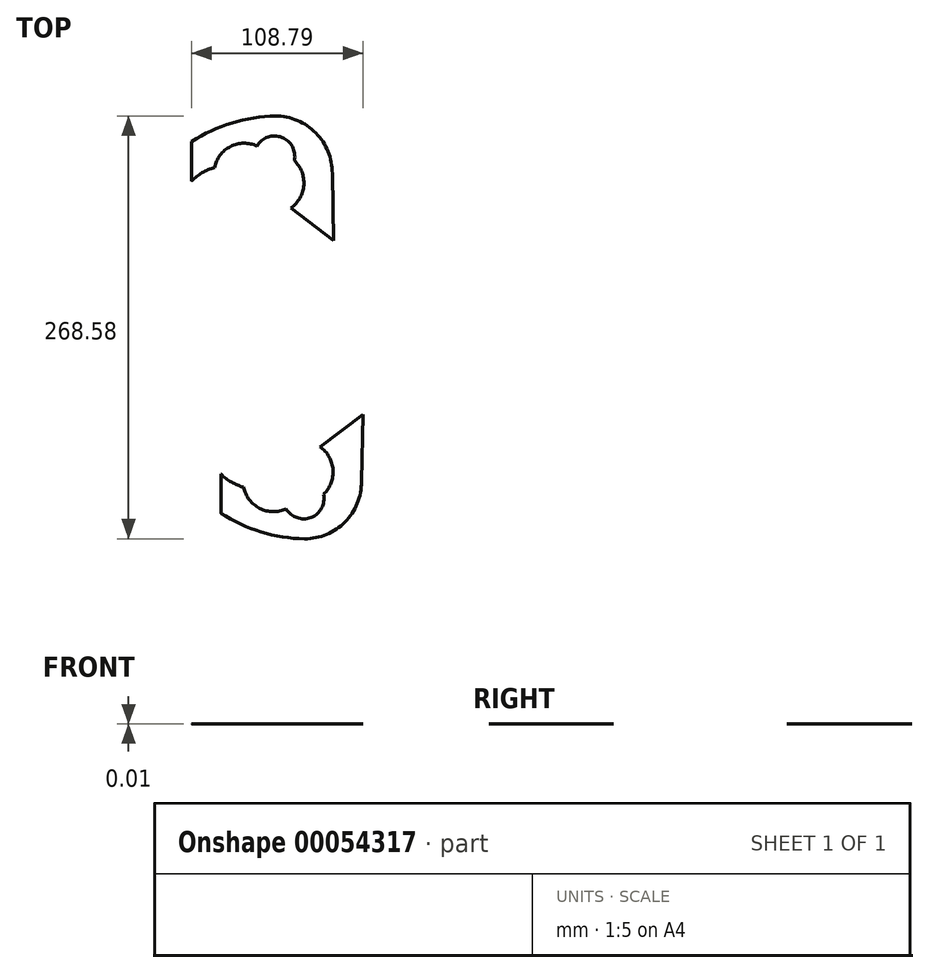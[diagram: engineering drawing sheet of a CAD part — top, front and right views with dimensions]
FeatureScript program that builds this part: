
annotation { "Feature Type Name" : "Feature", "Feature Type Description" : "" }
export const myFeature = defineFeature(function(context is Context, id is Id, definition is map)
    precondition{}
    {
        {
            var Q0;
            Q0=qCreatedBy(makeId("Top.planeOp"),FACE);
            var sketch = newSketch(context, id + "F0", { "sketchPlane" : qUnion([Q0])});
            skArc(sketch, "E0", {"start": v(11.73, -62.54) * mm, "mid": v(37.33, -51.81) * mm, "end": v(47.8, -26.1) * mm});
            skArc(sketch, "E1", {"start": v(23.7, -34.26) * mm, "mid": v(29.72, -18.68) * mm, "end": v(21.52, -4.14) * mm});
            skLineSegment(sketch, "E2", {"start": v(21.52, -4.14) * mm, "end": v(48.73, 16.61) * mm});
            skLineSegment(sketch, "E3", {"start": v(48.73, 16.61) * mm, "end": v(47.8, -26.1) * mm});
            skLineSegment(sketch, "E4", {"start": v(-49.43, -40.56) * mm, "end": v(-49.48, -6.1) * mm});
            skArc(sketch, "E5", {"start": v(-49.43, -40.56) * mm, "mid": v(-20.66, -56.57) * mm, "end": v(11.73, -62.54) * mm});
            skArc(sketch, "E6", {"start": v(-49.48, -6.1) * mm, "mid": v(-41.64, -21.15) * mm, "end": v(-26.98, -29.72) * mm});
            skArc(sketch, "E7", {"start": v(-26.98, -29.72) * mm, "mid": v(-16.84, -43.18) * mm, "end": v(0, -43.43) * mm});
            skArc(sketch, "E8", {"start": v(0, -43.43) * mm, "mid": v(15.77, -48.97) * mm, "end": v(23.7, -34.26) * mm});
            skSolve(sketch);
        }
        {
            var Q0;
            Q0 = qSketchRegion(id + "F0", true);
            extrude(context, id + "F1", {"entities" : qUnion([Q0]), "depth" : 5 / 406.4 * mm});
        }
        {
            var Q0;
            Q0=qCreatedBy(makeId("Top.planeOp"),FACE);
            var sketch = newSketch(context, id + "F2", { "sketchPlane" : qUnion([Q0])});
            skArc(sketch, "E9.MirrorCS", {"start": v(-18.54, 186.93) * mm, "mid": v(-2.77, 192.47) * mm, "end": v(5.16, 177.76) * mm});
            skArc(sketch, "E10.MirrorCS", {"start": v(-45.51, 173.23) * mm, "mid": v(-35.38, 186.68) * mm, "end": v(-18.54, 186.93) * mm});
            skArc(sketch, "E11.MirrorCS", {"start": v(-67.97, 184.06) * mm, "mid": v(-39.2, 200.07) * mm, "end": v(-6.8, 206.04) * mm});
            skLineSegment(sketch, "E12.MirrorCS", {"start": v(-67.97, 184.06) * mm, "end": v(-68.02, 149.6) * mm});
            skLineSegment(sketch, "E13.MirrorCS", {"start": v(30.2, 126.89) * mm, "end": v(29.26, 169.6) * mm});
            skLineSegment(sketch, "E14.MirrorCS", {"start": v(2.98, 147.64) * mm, "end": v(30.2, 126.89) * mm});
            skArc(sketch, "E15.MirrorCS", {"start": v(5.16, 177.76) * mm, "mid": v(11.19, 162.18) * mm, "end": v(2.98, 147.64) * mm});
            skArc(sketch, "E16.MirrorCS", {"start": v(-6.8, 206.04) * mm, "mid": v(18.8, 195.31) * mm, "end": v(29.26, 169.6) * mm});
            skArc(sketch, "E17.MirrorCS", {"start": v(-68.02, 149.6) * mm, "mid": v(-60.17, 164.65) * mm, "end": v(-45.51, 173.23) * mm});
            skSolve(sketch);
        }
        {
            var Q0;
            Q0 = qSketchRegion(id + "F2", true);
            extrude(context, id + "F3", {"entities" : qUnion([Q0]), "depth" : 5 / 406.4 * mm});
        }
        {
            var Q0;
            Q0=makeQuery(id+"F1.opExtrude","CAP_EDGE",EDGE,{"disambiguationData":[OSD([sQuery(id+"F0.wireOp",EDGE,"E4")])],"isStart":false});
            chamfer(context, id + "F4", {"entities" : qUnion([Q0]), "width" : 7.95 * mm, "tangentPropagation" : true});
        }
        {
            var Q0;
            Q0=makeQuery(id+"F3.opExtrude","CAP_EDGE",EDGE,{"disambiguationData":[OSD([sQuery(id+"F2.wireOp",EDGE,"E12.MirrorCS")])],"isStart":false});
            chamfer(context, id + "F5", {"entities" : qUnion([Q0]), "width" : 7.95 * mm, "tangentPropagation" : true});
        }
        {
            var Q0;
            Q0=makeQuery(id+"F1.opExtrude","SWEPT_FACE",FACE,{"disambiguationData":[OSD([sQuery(id+"F0.wireOp",EDGE,"E3")])]});
            var sketch = newSketch(context, id + "F6", { "sketchPlane" : qUnion([Q0])});
            skLineSegment(sketch, "E18.bottom", {"start": v(-25.05, 7.94) * mm, "end": v(17.67, 7.94) * mm});
            skLineSegment(sketch, "E18.top", {"start": v(-25.05, 2.32) * mm, "end": v(17.67, 2.32) * mm});
            skLineSegment(sketch, "E18.left", {"start": v(-25.05, 7.94) * mm, "end": v(-25.05, 2.32) * mm});
            skLineSegment(sketch, "E18.right", {"start": v(17.67, 7.94) * mm, "end": v(17.67, 2.32) * mm});
            skSolve(sketch);
        }
        {
            var Q0;
            Q0 = qSketchRegion(id + "F6", true);
            extrude(context, id + "F7", {"entities" : qUnion([Q0]), "operationType" : NewBodyOperationType.REMOVE, "oppositeDirection" : true, "depth" : 27.7 * mm});
        }
        {
            var Q0;
            Q0=makeQuery(id+"F3.opExtrude","SWEPT_FACE",FACE,{"disambiguationData":[OSD([sQuery(id+"F2.wireOp",EDGE,"E13.MirrorCS")])]});
            var sketch = newSketch(context, id + "F8", { "sketchPlane" : qUnion([Q0])});
            skLineSegment(sketch, "E19.bottom", {"start": v(168.92, 7.94) * mm, "end": v(126.2, 7.94) * mm});
            skLineSegment(sketch, "E19.top", {"start": v(168.92, 2.07) * mm, "end": v(126.2, 2.07) * mm});
            skLineSegment(sketch, "E19.left", {"start": v(168.92, 7.94) * mm, "end": v(168.92, 2.07) * mm});
            skLineSegment(sketch, "E19.right", {"start": v(126.2, 7.94) * mm, "end": v(126.2, 2.07) * mm});
            skSolve(sketch);
        }
        {
            var Q0;
            Q0 = qSketchRegion(id + "F8", true);
            extrude(context, id + "F9", {"entities" : qUnion([Q0]), "operationType" : NewBodyOperationType.REMOVE, "oppositeDirection" : true, "depth" : 27.94 * mm});
        }
    });
